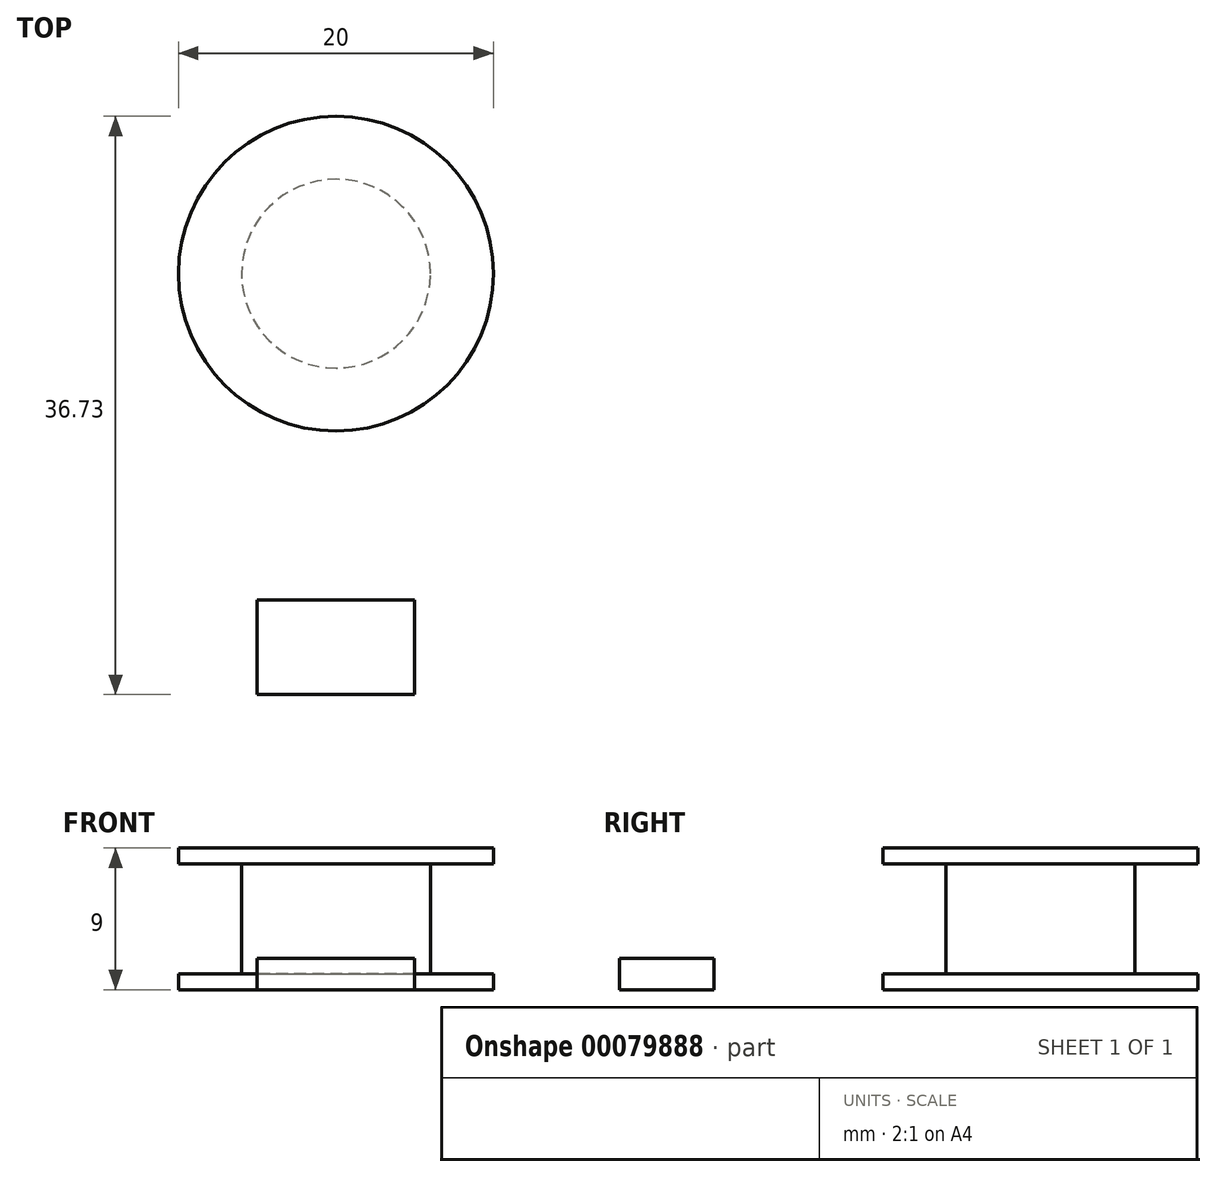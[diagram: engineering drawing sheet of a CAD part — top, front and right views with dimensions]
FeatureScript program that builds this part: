
annotation { "Feature Type Name" : "Feature", "Feature Type Description" : "" }
export const myFeature = defineFeature(function(context is Context, id is Id, definition is map)
    precondition{}
    {
        {
            var Q0;
            Q0=qCreatedBy(makeId("Top.planeOp"),FACE);
            var sketch = newSketch(context, id + "F0", { "sketchPlane" : qUnion([Q0])});
            skLineSegment(sketch, "E0.bottom", {"start": v(5, -3) * mm, "end": v(-5, -3) * mm});
            skLineSegment(sketch, "E0.top", {"start": v(5, 3) * mm, "end": v(-5, 3) * mm});
            skLineSegment(sketch, "E0.left", {"start": v(5, -3) * mm, "end": v(5, 3) * mm});
            skLineSegment(sketch, "E0.right", {"start": v(-5, -3) * mm, "end": v(-5, 3) * mm});
            skPoint(sketch, "E0.middle", {"position": v(0, 0) * mm});
            skCircle(sketch, "E1", {"center": v(0, 23.73) * mm, "radius": 10 * mm});
            skLineSegment(sketch, "E2", {"start": v(0, 0) * mm, "end": v(0, 23.73) * mm, "construction": true});
            skSolve(sketch);
        }
        {
            var Q0;
            Q0 = qSketchRegion(id + "F0", true);
            var Q1;
            Q1=makeQuery(id+"F0.imprint","IMPRINT",FACE,{"disambiguationData":[TD([[makeQuery(id+"F0.imprint","IMPRINT",EDGE,{"derivedFrom":sQuery(id+"F0.wireOp",EDGE,"E0.bottom")}),-1.0]])]});
            extrude(context, id + "F1", {"entities" : qUnion([Q0, Q1]), "depth" : 2 * mm});
        }
        {
            var Q0;
            Q0=makeQuery(id+"F1.opExtrude","CAP_FACE",FACE,{"disambiguationData":[OSD([sQuery(id+"F0.wireOp",EDGE,"E1")])],"isStart":false});
            extrude(context, id + "F2", {"entities" : qUnion([Q0]), "operationType" : NewBodyOperationType.ADD, "depth" : 7 * mm});
        }
        {
            var Q0;
            Q0=qCreatedBy(makeId("Right.planeOp"),FACE);
            var sketch = newSketch(context, id + "F3", { "sketchPlane" : qUnion([Q0])});
            skLineSegment(sketch, "E3.0", {"start": v(13.73, 9) * mm, "end": v(33.73, 9) * mm});
            skLineSegment(sketch, "E3.1", {"start": v(13.73, 0) * mm, "end": v(33.73, 0) * mm});
            skLineSegment(sketch, "E4.bottom", {"start": v(33.73, 9) * mm, "end": v(13.73, 9) * mm});
            skLineSegment(sketch, "E4.top", {"start": v(33.73, 0) * mm, "end": v(13.73, 0) * mm});
            skLineSegment(sketch, "E4.left", {"start": v(33.73, 9) * mm, "end": v(33.73, 0) * mm});
            skLineSegment(sketch, "E4.right", {"start": v(13.73, 9) * mm, "end": v(13.73, 0) * mm});
            skLineSegment(sketch, "E5.left", {"start": v(33.73, 8) * mm, "end": v(33.73, 1) * mm});
            skLineSegment(sketch, "E5.right", {"start": v(13.73, 8) * mm, "end": v(13.73, 1) * mm});
            skLineSegment(sketch, "E6.left", {"start": v(13.73, 1) * mm, "end": v(13.73, 8) * mm});
            skLineSegment(sketch, "E7.bottom", {"start": v(33.73, 8) * mm, "end": v(29.73, 8) * mm});
            skLineSegment(sketch, "E7.top", {"start": v(33.73, 1) * mm, "end": v(29.73, 1) * mm});
            skLineSegment(sketch, "E7.right", {"start": v(29.73, 8) * mm, "end": v(29.73, 1) * mm});
            skLineSegment(sketch, "E8", {"start": v(23.73, 9) * mm, "end": v(23.73, 0) * mm, "construction": true});
            skSolve(sketch);
        }
        {
            var Q0;
            Q0=makeQuery(id+"F3.imprint","IMPRINT",FACE,{"disambiguationData":[TD([[makeQuery(id+"F3.imprint","IMPRINT",EDGE,{"derivedFrom":sQuery(id+"F3.wireOp",EDGE,"E7.bottom")}),1.0]])]});
            var Q1;
            Q1=sQuery(id+"F3.wireOp",EDGE,"E8");
            revolve(context, id + "F4", {"operationType" : NewBodyOperationType.REMOVE, "entities" : qUnion([Q0]), "axis" : qUnion([Q1]), "revolveType" : RevolveType.FULL, "oppositeDirection" : true});
        }
    });
